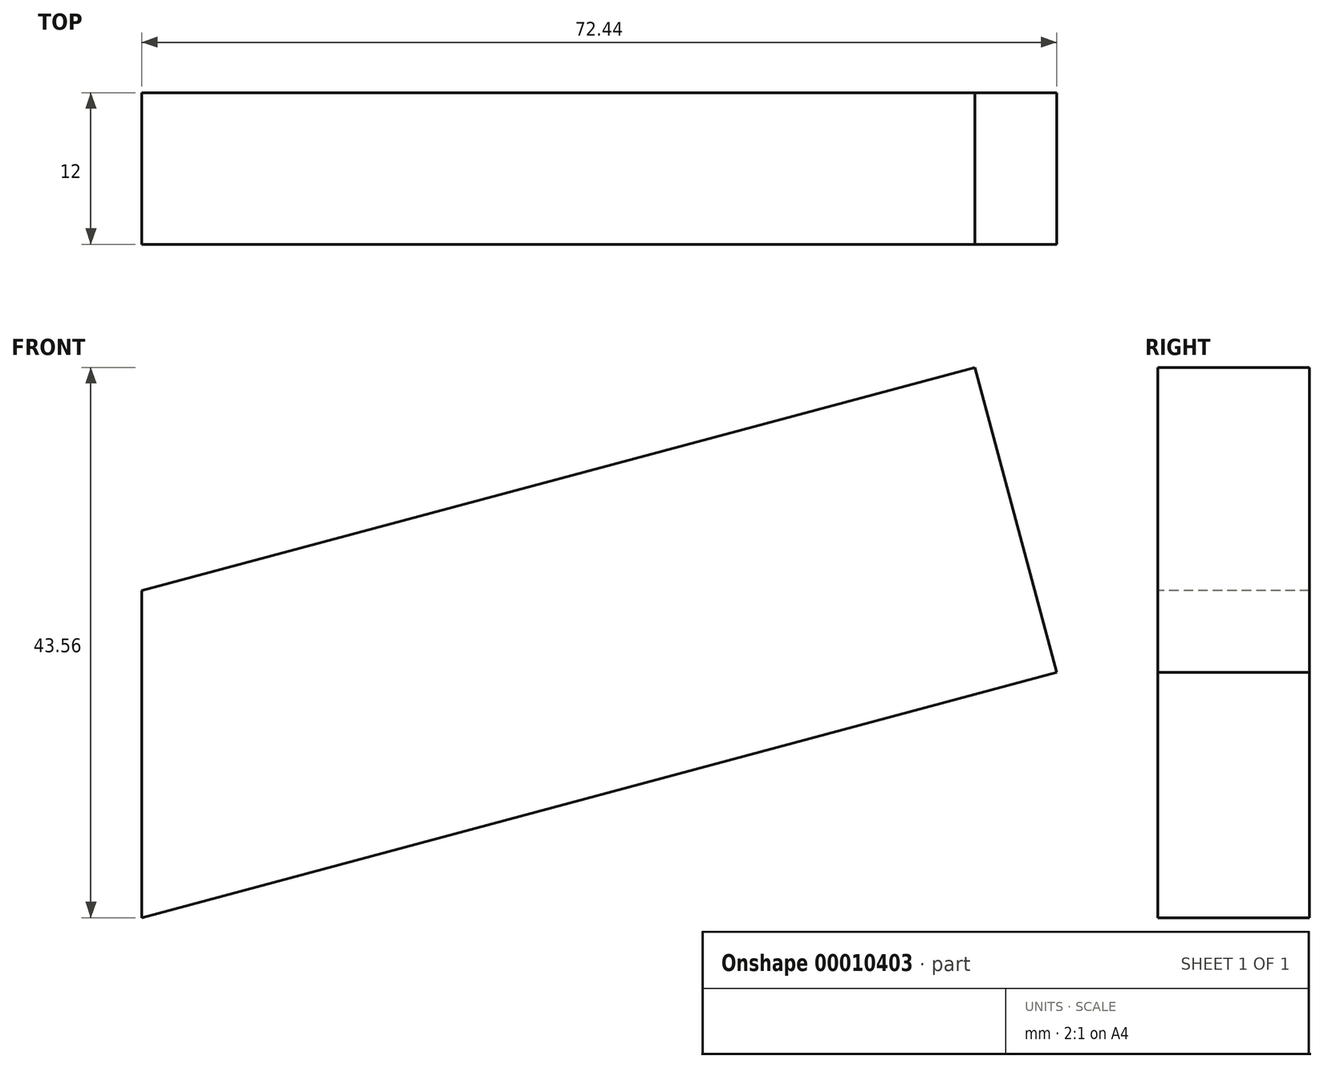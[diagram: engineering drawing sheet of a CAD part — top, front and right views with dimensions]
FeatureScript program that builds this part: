
annotation { "Feature Type Name" : "Feature", "Feature Type Description" : "" }
export const myFeature = defineFeature(function(context is Context, id is Id, definition is map)
    precondition{}
    {
        {
            var Q0;
            Q0=qCreatedBy(makeId("Front.planeOp"),FACE);
            var sketch = newSketch(context, id + "F0", { "sketchPlane" : qUnion([Q0])});
            skLineSegment(sketch, "E0", {"start": v(0, 0) * mm, "end": v(0, 25.88) * mm});
            skLineSegment(sketch, "E1", {"start": v(0, 25.88) * mm, "end": v(65.97, 43.56) * mm});
            skLineSegment(sketch, "E2", {"start": v(65.97, 43.56) * mm, "end": v(72.44, 19.41) * mm});
            skLineSegment(sketch, "E3", {"start": v(72.44, 19.41) * mm, "end": v(0, 0) * mm});
            skSolve(sketch);
        }
        {
            var Q0;
            Q0 = qSketchRegion(id + "F0", true);
            extrude(context, id + "F1", {"entities" : qUnion([Q0]), "oppositeDirection" : true, "depth" : 12 * mm});
        }
    });
